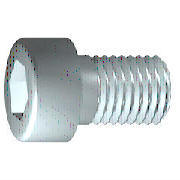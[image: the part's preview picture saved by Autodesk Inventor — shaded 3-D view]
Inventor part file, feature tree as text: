
AUTODESK INVENTOR PART (.ipt)
format: ipt  version: 2024 (Build 280153000, 153)  size: 188,928 bytes
history: native  units: mm (DEFAULTED — no unit token found)
features: fillet x2, sketch x2, extrude x1, thread x1, chamfer x1, plane x1
ambient origin geometry x7: Origin, YZ Plane, XY Plane, X Axis, Y Axis, Z Axis, Center Point
bodies: Solid1 (feature_tree), Body (feature_tree)
feature tree (8):
  extrude  "Slot"  Depth=3.0mm
  fillet  "Fillet1"  Radius=3.0mm
  thread  "Thread"  [1 undecoded]
  chamfer  "Chamfer1"  Distance=3.0mm
  plane  "Work Plane1"
  fillet  "Fillet2"  Radius=3.0mm
  sketch  "Sketch1"  dims[d1=14.75mm d2=0.306825mm d3=3.0mm d4=1.3mm]
  sketch  "Sketch2"  dims[d5=60.0deg d6=3.0mm d7=3.0mm d8=2.886751mm d9=5.5mm d10=90.0deg d11=10.0mm d12=0.0mm d13=14.75mm d14=0.0mm d15=0.306725mm d16=0.306725mm d17=0.3mm d19=0.0mm d26=16.0mm d27=45.0deg d28=0.0mm d29=0.0mm d30=0.1mm]
note: 1 required parameter value undecoded (feature->parameter linkage not recoverable at this tier; creation-order binding heuristic only, values carry confidence <= 0.55)
